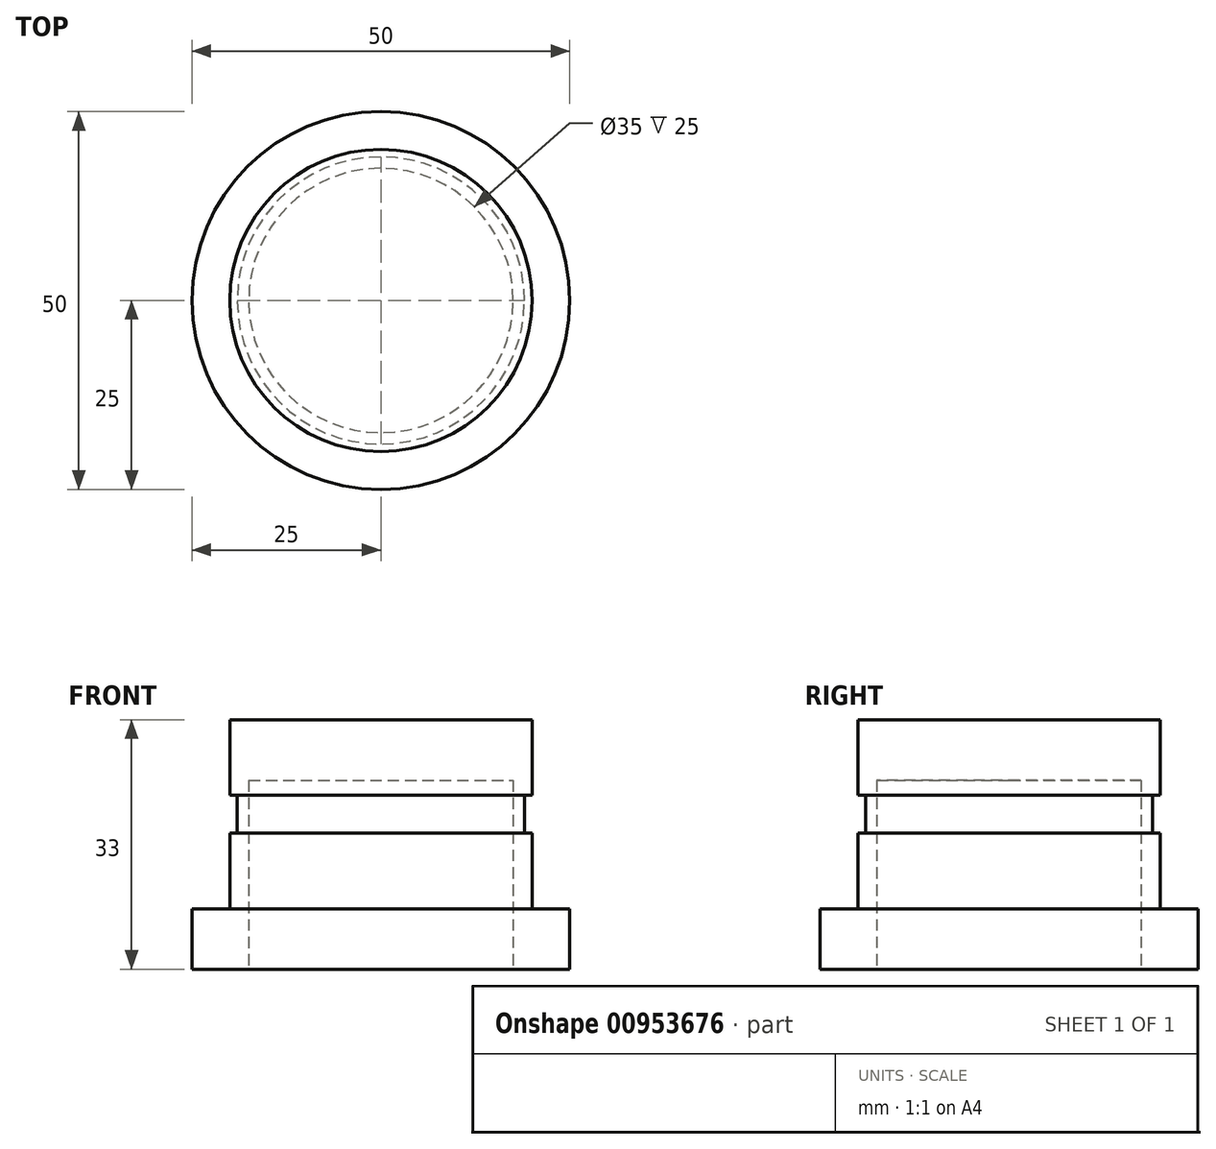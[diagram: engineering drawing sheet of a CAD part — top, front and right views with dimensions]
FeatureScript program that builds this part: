
annotation { "Feature Type Name" : "Feature", "Feature Type Description" : "" }
export const myFeature = defineFeature(function(context is Context, id is Id, definition is map)
    precondition{}
    {
        {
            var Q0;
            Q0=qCreatedBy(makeId("Top.planeOp"),FACE);
            var sketch = newSketch(context, id + "F0", { "sketchPlane" : qUnion([Q0])});
            skCircle(sketch, "E0", {"center": v(0, 0) * mm, "radius": 25 * mm});
            skSolve(sketch);
        }
        {
            var Q0;
            Q0=qSketchRegion(id+"F0",true);
            extrude(context, id + "F1", {"entities" : qUnion([Q0]), "depth" : 8 * mm, "offsetDistance" : 25 * mm});
        }
        {
            var Q0;
            Q0=makeQuery(id+"F1.opExtrude","CAP_FACE",FACE,{"disambiguationData":[OSD([sQuery(id+"F0.wireOp",EDGE,"E0")])],"isStart":false});
            var sketch = newSketch(context, id + "F2", { "sketchPlane" : qUnion([Q0])});
            skCircle(sketch, "E1", {"center": v(0, 0) * mm, "radius": 20 * mm});
            skSolve(sketch);
        }
        {
            var Q0;
            Q0=qSketchRegion(id+"F2",true);
            extrude(context, id + "F3", {"entities" : qUnion([Q0]), "operationType" : NewBodyOperationType.ADD, "depth" : 10 * mm, "offsetDistance" : 25 * mm});
        }
        {
            var Q0;
            Q0=makeQuery(id+"F3.opExtrude","CAP_FACE",FACE,{"disambiguationData":[OSD([sQuery(id+"F2.wireOp",EDGE,"E1")])],"isStart":false});
            var sketch = newSketch(context, id + "F4", { "sketchPlane" : qUnion([Q0])});
            skCircle(sketch, "E2", {"center": v(0, 0) * mm, "radius": 19 * mm});
            skSolve(sketch);
        }
        {
            var Q0;
            Q0=qSketchRegion(id+"F4",true);
            extrude(context, id + "F5", {"entities" : qUnion([Q0]), "operationType" : NewBodyOperationType.ADD, "depth" : 5 * mm, "offsetDistance" : 25 * mm});
        }
        {
            var Q0;
            Q0=makeQuery(id+"F5.opExtrude","CAP_FACE",FACE,{"disambiguationData":[OSD([sQuery(id+"F4.wireOp",EDGE,"E2")])],"isStart":false});
            var sketch = newSketch(context, id + "F6", { "sketchPlane" : qUnion([Q0])});
            skCircle(sketch, "E3", {"center": v(0, 0) * mm, "radius": 20 * mm});
            skSolve(sketch);
        }
        {
            var Q0;
            Q0=qSketchRegion(id+"F6",true);
            extrude(context, id + "F7", {"entities" : qUnion([Q0]), "operationType" : NewBodyOperationType.ADD, "depth" : 10 * mm, "offsetDistance" : 25 * mm});
        }
        {
            var Q0;
            Q0=makeQuery(id+"F1.opExtrude","CAP_FACE",FACE,{"disambiguationData":[OSD([sQuery(id+"F0.wireOp",EDGE,"E0")])],"isStart":true});
            var sketch = newSketch(context, id + "F8", { "sketchPlane" : qUnion([Q0])});
            skCircle(sketch, "E4", {"center": v(0, 0) * mm, "radius": 17.5 * mm});
            skSolve(sketch);
        }
        {
            var Q0;
            Q0=qSketchRegion(id+"F8",true);
            extrude(context, id + "F9", {"entities" : qUnion([Q0]), "operationType" : NewBodyOperationType.REMOVE, "oppositeDirection" : true, "depth" : 25 * mm, "offsetDistance" : 25 * mm});
        }
    });
